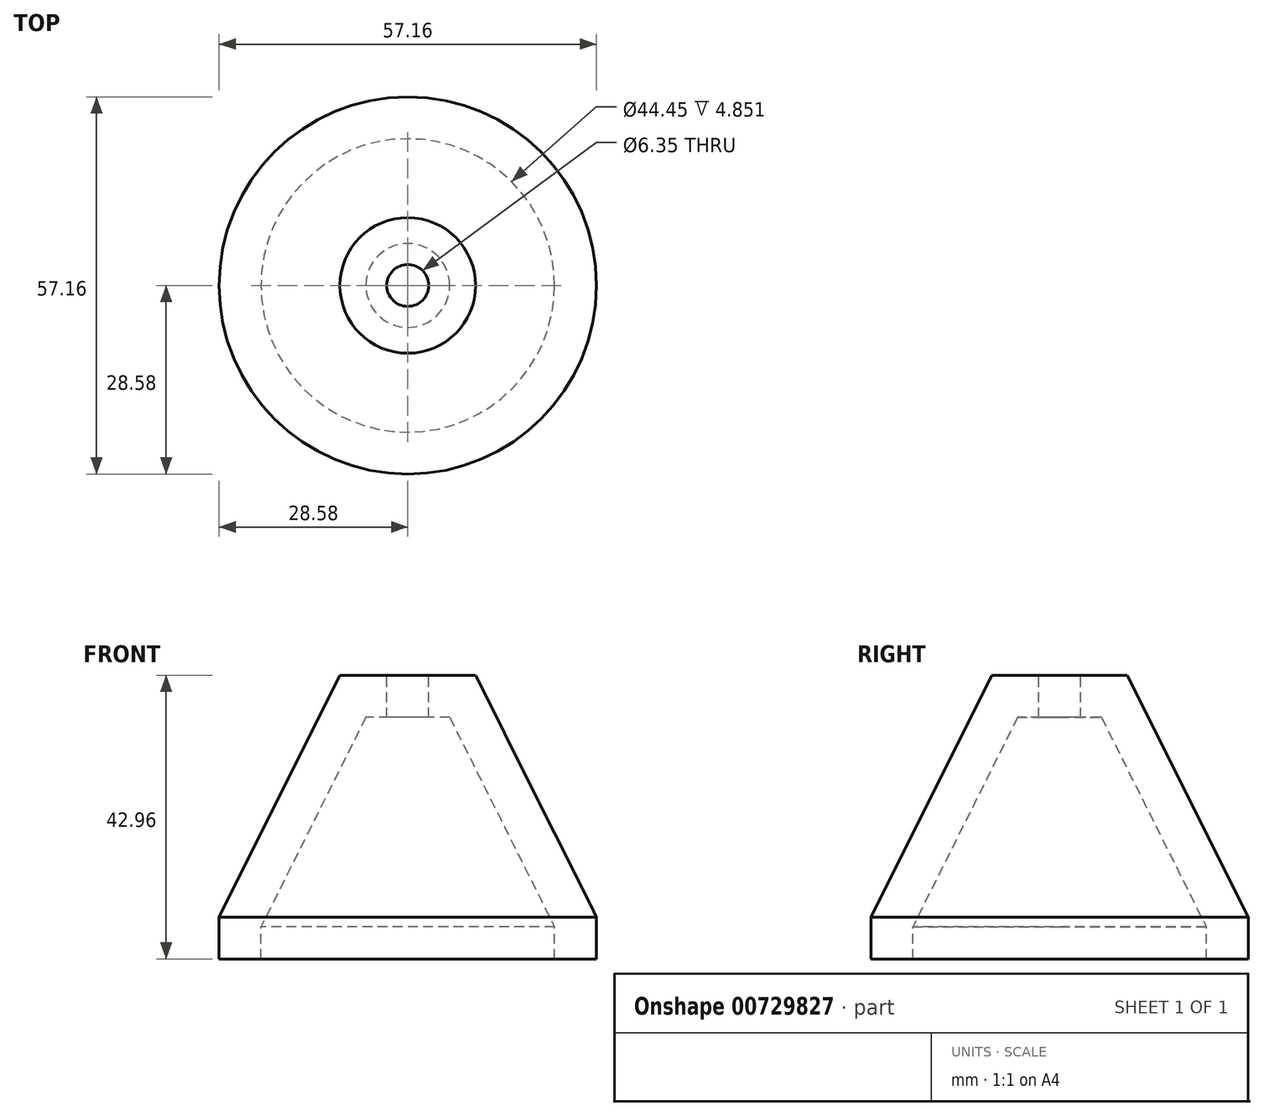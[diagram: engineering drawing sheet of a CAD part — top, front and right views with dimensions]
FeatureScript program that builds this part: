
annotation { "Feature Type Name" : "Feature", "Feature Type Description" : "" }
export const myFeature = defineFeature(function(context is Context, id is Id, definition is map)
    precondition{}
    {
        {
            var Q0;
            Q0=qCreatedBy(makeId("Front.planeOp"),FACE);
            var sketch = newSketch(context, id + "F0", { "sketchPlane" : qUnion([Q0])});
            skLineSegment(sketch, "E0", {"start": v(22.23, 3.92) * mm, "end": v(28.58, 3.92) * mm});
            skLineSegment(sketch, "E1", {"start": v(10.27, 46.88) * mm, "end": v(3.17, 46.88) * mm});
            skLineSegment(sketch, "E2", {"start": v(28.58, 10.27) * mm, "end": v(28.58, 3.92) * mm});
            skLineSegment(sketch, "E3", {"start": v(28.58, 10.27) * mm, "end": v(10.27, 46.88) * mm});
            skPoint(sketch, "E4.start.orphan", {"position": v(25.6, 10.27) * mm});
            skPoint(sketch, "E5.start.orphan", {"position": v(-11.4, 0) * mm});
            skLineSegment(sketch, "E6.0", {"start": v(22.23, 8.78) * mm, "end": v(6.35, 40.53) * mm});
            skLineSegment(sketch, "E7.0", {"start": v(6.35, 40.53) * mm, "end": v(3.18, 40.53) * mm});
            skLineSegment(sketch, "E8.0", {"start": v(22.23, 8.78) * mm, "end": v(22.23, 3.92) * mm});
            skLineSegment(sketch, "E9", {"start": v(3.18, 40.53) * mm, "end": v(3.17, 46.88) * mm});
            skPoint(sketch, "E10.orphan", {"position": v(0, 46.88) * mm});
            skPoint(sketch, "E11.start.orphan", {"position": v(0, 40.53) * mm});
            skLineSegment(sketch, "E12", {"start": v(0, 46.88) * mm, "end": v(0, 40.53) * mm});
            skSolve(sketch);
        }
        {
            var Q0;
            Q0=makeQuery(id+"F0.imprint","IMPRINT",FACE,{"disambiguationData":[TD([[makeQuery(id+"F0.imprint","IMPRINT",EDGE,{"derivedFrom":sQuery(id+"F0.wireOp",EDGE,"E0")}),1.0]])]});
            var Q1;
            Q1=sQuery(id+"F0.wireOp",EDGE,"E12");
            revolve(context, id + "F1", {"surfaceOperationType" : NewSurfaceOperationType.NEW, "entities" : qUnion([Q0]), "axis" : qUnion([Q1]), "revolveType" : RevolveType.FULL});
        }
    });
